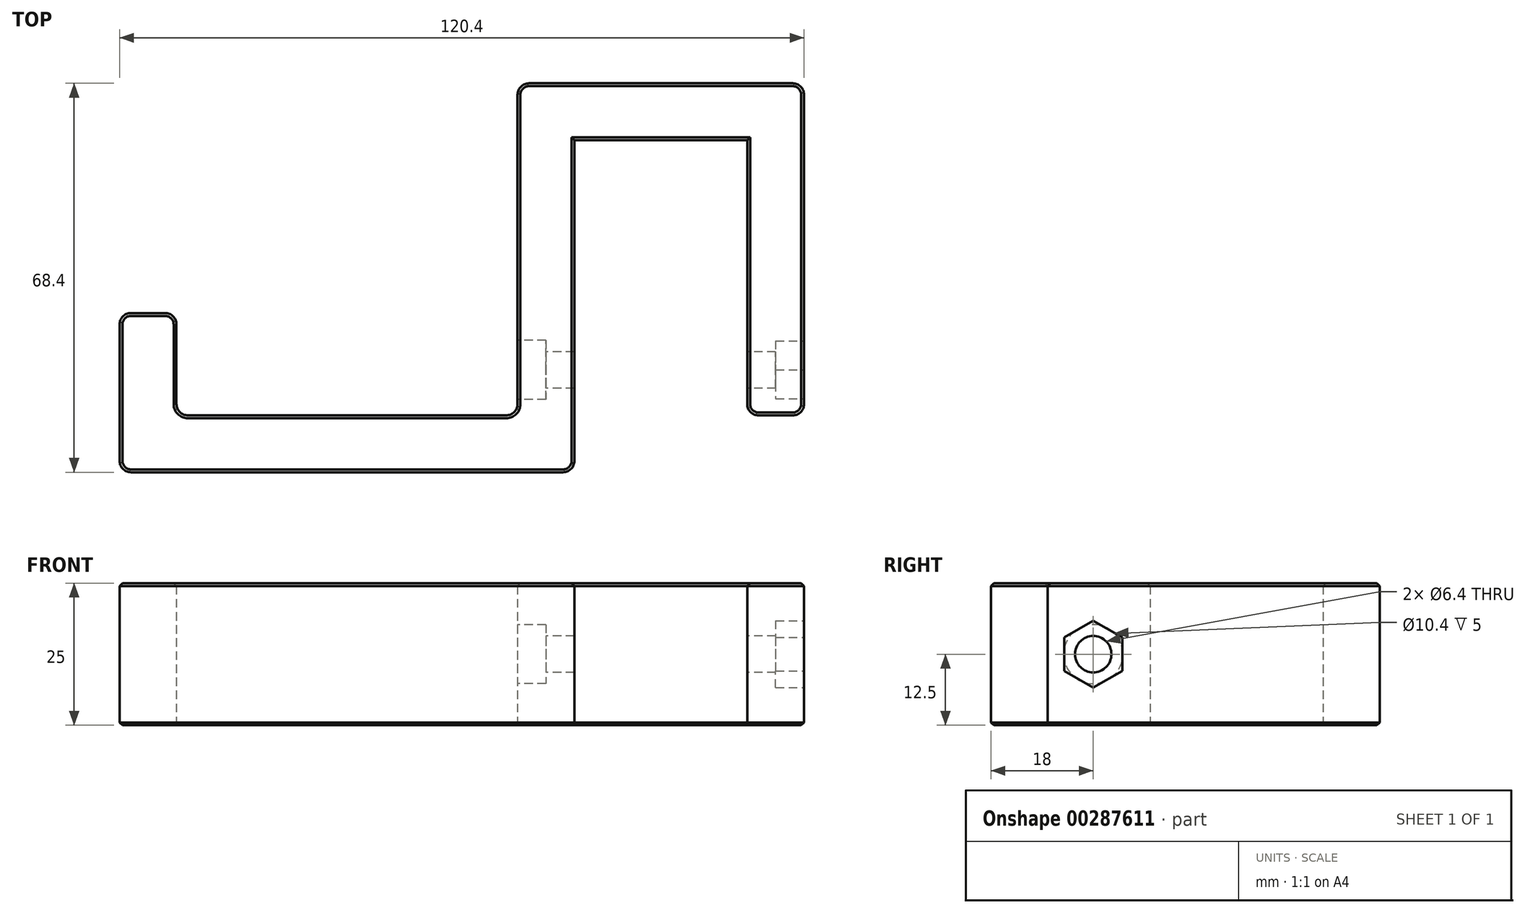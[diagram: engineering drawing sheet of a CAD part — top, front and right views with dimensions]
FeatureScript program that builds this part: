
annotation { "Feature Type Name" : "Feature", "Feature Type Description" : "" }
export const myFeature = defineFeature(function(context is Context, id is Id, definition is map)
    precondition{}
    {
        {
            var Q0;
            Q0=qCreatedBy(makeId("Top.planeOp"),FACE);
            var sketch = newSketch(context, id + "F0", { "sketchPlane" : qUnion([Q0])});
            skLineSegment(sketch, "E0.bottom", {"start": v(15.2, -15.2) * mm, "end": v(-15.2, -15.2) * mm, "construction": true});
            skLineSegment(sketch, "E0.top", {"start": v(15.2, 15.2) * mm, "end": v(-15.2, 15.2) * mm, "construction": true});
            skLineSegment(sketch, "E0.left", {"start": v(15.2, -15.2) * mm, "end": v(15.2, 15.2) * mm, "construction": true});
            skLineSegment(sketch, "E0.right", {"start": v(-15.2, -15.2) * mm, "end": v(-15.2, 15.2) * mm, "construction": true});
            skPoint(sketch, "E0.middle", {"position": v(0, 0) * mm});
            skLineSegment(sketch, "E1", {"start": v(15.2, 15.2) * mm, "end": v(15.2, -33.2) * mm});
            skLineSegment(sketch, "E2", {"start": v(15.2, -33.2) * mm, "end": v(25.2, -33.2) * mm});
            skLineSegment(sketch, "E3", {"start": v(25.2, -33.2) * mm, "end": v(25.2, 25.2) * mm});
            skLineSegment(sketch, "E4", {"start": v(25.2, 25.2) * mm, "end": v(-25.2, 25.2) * mm});
            skLineSegment(sketch, "E5", {"start": v(-25.2, 25.2) * mm, "end": v(-25.2, -33.2) * mm});
            skLineSegment(sketch, "E6", {"start": v(-25.2, -33.2) * mm, "end": v(-15.2, -33.2) * mm});
            skLineSegment(sketch, "E7", {"start": v(-15.2, -33.2) * mm, "end": v(-15.2, 15.2) * mm});
            skLineSegment(sketch, "E8.bottom", {"start": v(-15.2, -33.2) * mm, "end": v(-95.2, -33.2) * mm});
            skLineSegment(sketch, "E8.top", {"start": v(-15.2, -43.2) * mm, "end": v(-95.2, -43.2) * mm});
            skLineSegment(sketch, "E8.left", {"start": v(-15.2, -33.2) * mm, "end": v(-15.2, -43.2) * mm});
            skLineSegment(sketch, "E8.right", {"start": v(-95.2, -33.2) * mm, "end": v(-95.2, -43.2) * mm});
            skLineSegment(sketch, "E9.bottom", {"start": v(-95.2, -33.2) * mm, "end": v(-85.2, -33.2) * mm});
            skLineSegment(sketch, "E9.top", {"start": v(-95.2, -15.2) * mm, "end": v(-85.2, -15.2) * mm});
            skLineSegment(sketch, "E9.left", {"start": v(-95.2, -33.2) * mm, "end": v(-95.2, -15.2) * mm});
            skLineSegment(sketch, "E9.right", {"start": v(-85.2, -33.2) * mm, "end": v(-85.2, -15.2) * mm});
            skLineSegment(sketch, "E10", {"start": v(-15.2, 15.2) * mm, "end": v(15.2, 15.2) * mm});
            skSolve(sketch);
        }
        {
            var Q0;
            Q0=qSketchRegion(id+"F0",true);
            extrude(context, id + "F1", {"entities" : qUnion([Q0]), "depth" : 25 * mm, "offsetDistance" : 25 * mm});
        }
        {
            var Q0;
            Q0=makeQuery(id+"F1.opExtrude","SWEPT_FACE",FACE,{"disambiguationData":[OSD([sQuery(id+"F0.wireOp",EDGE,"E5")])]});
            var sketch = newSketch(context, id + "F2", { "sketchPlane" : qUnion([Q0])});
            skPoint(sketch, "E11", {"position": v(33.2, 12.5) * mm});
            skCircle(sketch, "E12", {"center": v(25.2, 12.5) * mm, "radius": 3.2 * mm});
            skCircle(sketch, "E13", {"center": v(25.2, 12.5) * mm, "radius": 5.2 * mm});
            skSolve(sketch);
        }
        {
            var Q0;
            Q0=makeQuery(id+"F2.imprint","IMPRINT",FACE,{"disambiguationData":[TD([[makeQuery(id+"F2.imprint","IMPRINT",EDGE,{"derivedFrom":sQuery(id+"F2.wireOp",EDGE,"E12")}),1.0]])]});
            extrude(context, id + "F3", {"entities" : qUnion([Q0]), "operationType" : NewBodyOperationType.REMOVE, "endBound" : BoundingType.THROUGH_ALL, "oppositeDirection" : true, "depth" : 25 * mm, "offsetDistance" : 25 * mm});
        }
        {
            var Q0;
            Q0=makeQuery(id+"F2.imprint","IMPRINT",FACE,{"disambiguationData":[TD([[makeQuery(id+"F2.imprint","IMPRINT",EDGE,{"derivedFrom":sQuery(id+"F2.wireOp",EDGE,"E12")}),-1.0]])]});
            extrude(context, id + "F4", {"entities" : qUnion([Q0]), "operationType" : NewBodyOperationType.REMOVE, "oppositeDirection" : true, "depth" : 5 * mm, "offsetDistance" : 25 * mm});
        }
        {
            var Q0;
            Q0=makeQuery(id+"F1.opExtrude","SWEPT_FACE",FACE,{"disambiguationData":[OSD([sQuery(id+"F0.wireOp",EDGE,"E3")])]});
            var sketch = newSketch(context, id + "F5", { "sketchPlane" : qUnion([Q0])});
            skCircle(sketch, "E14.cCircle", {"center": v(-25.2, 12.5) * mm, "radius": 5.1 * mm, "construction": true});
            skLineSegment(sketch, "E14.0", {"start": v(-25.2, 6.61) * mm, "end": v(-30.3, 9.56) * mm});
            skLineSegment(sketch, "E14.1", {"start": v(-30.3, 9.56) * mm, "end": v(-30.3, 15.44) * mm});
            skLineSegment(sketch, "E14.2", {"start": v(-30.3, 15.44) * mm, "end": v(-25.2, 18.39) * mm});
            skLineSegment(sketch, "E14.3", {"start": v(-25.2, 18.39) * mm, "end": v(-20.1, 15.44) * mm});
            skLineSegment(sketch, "E14.4", {"start": v(-20.1, 15.44) * mm, "end": v(-20.1, 9.56) * mm});
            skLineSegment(sketch, "E14.5", {"start": v(-20.1, 9.56) * mm, "end": v(-25.2, 6.61) * mm});
            skPoint(sketch, "E14.0.midPoint", {"position": v(-27.75, 8.08) * mm});
            skSolve(sketch);
        }
        {
            var Q0;
            Q0=makeQuery(id+"F5.imprint","IMPRINT",FACE,{"disambiguationData":[TD([[makeQuery(id+"F5.imprint","IMPRINT",EDGE,{"derivedFrom":sQuery(id+"F5.wireOp",EDGE,"E14.0")}),-1.0]])]});
            extrude(context, id + "F6", {"entities" : qUnion([Q0]), "operationType" : NewBodyOperationType.REMOVE, "oppositeDirection" : true, "depth" : 5 * mm, "offsetDistance" : 25 * mm});
        }
        {
            var Q0;
            Q0=makeQuery(id+"F1.opExtrude","SWEPT_EDGE",EDGE,{"disambiguationData":[OSD([sQuery(id+"F0.wireOp",EDGE,"E5"),sQuery(id+"F0.wireOp",EDGE,"E8.bottom")])]});
            var Q1;
            Q1=makeQuery(id+"F1.opExtrude","SWEPT_EDGE",EDGE,{"disambiguationData":[OSD([sQuery(id+"F0.wireOp",EDGE,"E8.top"),sQuery(id+"F0.wireOp",EDGE,"E8.left")])]});
            var Q2;
            Q2=makeQuery(id+"F1.opExtrude","SWEPT_EDGE",EDGE,{"disambiguationData":[OSD([sQuery(id+"F0.wireOp",EDGE,"E2"),sQuery(id+"F0.wireOp",EDGE,"E1")])]});
            var Q3;
            Q3=makeQuery(id+"F1.opExtrude","SWEPT_EDGE",EDGE,{"disambiguationData":[OSD([sQuery(id+"F0.wireOp",EDGE,"E2"),sQuery(id+"F0.wireOp",EDGE,"E3")])]});
            var Q4;
            Q4=makeQuery(id+"F1.opExtrude","SWEPT_EDGE",EDGE,{"disambiguationData":[OSD([sQuery(id+"F0.wireOp",EDGE,"E3"),sQuery(id+"F0.wireOp",EDGE,"E4")])]});
            var Q5;
            Q5=makeQuery(id+"F1.opExtrude","SWEPT_EDGE",EDGE,{"disambiguationData":[OSD([sQuery(id+"F0.wireOp",EDGE,"E8.bottom"),sQuery(id+"F0.wireOp",EDGE,"E9.bottom"),sQuery(id+"F0.wireOp",EDGE,"E9.right")])]});
            var Q6;
            Q6=makeQuery(id+"F1.opExtrude","SWEPT_EDGE",EDGE,{"disambiguationData":[OSD([sQuery(id+"F0.wireOp",EDGE,"E9.top"),sQuery(id+"F0.wireOp",EDGE,"E9.right")])]});
            var Q7;
            Q7=makeQuery(id+"F1.opExtrude","SWEPT_EDGE",EDGE,{"disambiguationData":[OSD([sQuery(id+"F0.wireOp",EDGE,"E9.top"),sQuery(id+"F0.wireOp",EDGE,"E9.left")])]});
            var Q8;
            Q8=makeQuery(id+"F1.opExtrude","SWEPT_EDGE",EDGE,{"disambiguationData":[OSD([sQuery(id+"F0.wireOp",EDGE,"E8.top"),sQuery(id+"F0.wireOp",EDGE,"E8.right")])]});
            var Q9;
            Q9=makeQuery(id+"F1.opExtrude","SWEPT_EDGE",EDGE,{"disambiguationData":[OSD([sQuery(id+"F0.wireOp",EDGE,"E4"),sQuery(id+"F0.wireOp",EDGE,"E5")])]});
            fillet(context, id + "F7", {"entities" : qUnion([Q0, Q1, Q2, Q3, Q4, Q5, Q6, Q7, Q8, Q9]), "tangentPropagation" : true, "radius" : 2 * mm, "defaultsChanged" : false, "vertexSettings" : [], "allowEdgeOverflow" : false});
        }
        {
            var Q0;
            Q0=makeQuery(id+"F1.opExtrude","CAP_FACE",FACE,{"disambiguationData":[OSD([sQuery(id+"F0.wireOp",EDGE,"E2"),sQuery(id+"F0.wireOp",EDGE,"E3"),sQuery(id+"F0.wireOp",EDGE,"E4"),sQuery(id+"F0.wireOp",EDGE,"E5"),sQuery(id+"F0.wireOp",EDGE,"E7"),sQuery(id+"F0.wireOp",EDGE,"E1"),sQuery(id+"F0.wireOp",EDGE,"E8.bottom"),sQuery(id+"F0.wireOp",EDGE,"E8.top"),sQuery(id+"F0.wireOp",EDGE,"E8.left"),sQuery(id+"F0.wireOp",EDGE,"E8.right"),sQuery(id+"F0.wireOp",EDGE,"E9.top"),sQuery(id+"F0.wireOp",EDGE,"E9.left"),sQuery(id+"F0.wireOp",EDGE,"E9.right"),sQuery(id+"F0.wireOp",EDGE,"E10")])],"isStart":false});
            var Q1;
            Q1=makeQuery(id+"F1.opExtrude","CAP_FACE",FACE,{"disambiguationData":[OSD([sQuery(id+"F0.wireOp",EDGE,"E2"),sQuery(id+"F0.wireOp",EDGE,"E3"),sQuery(id+"F0.wireOp",EDGE,"E4"),sQuery(id+"F0.wireOp",EDGE,"E5"),sQuery(id+"F0.wireOp",EDGE,"E7"),sQuery(id+"F0.wireOp",EDGE,"E1"),sQuery(id+"F0.wireOp",EDGE,"E8.bottom"),sQuery(id+"F0.wireOp",EDGE,"E8.top"),sQuery(id+"F0.wireOp",EDGE,"E8.left"),sQuery(id+"F0.wireOp",EDGE,"E8.right"),sQuery(id+"F0.wireOp",EDGE,"E9.top"),sQuery(id+"F0.wireOp",EDGE,"E9.left"),sQuery(id+"F0.wireOp",EDGE,"E9.right"),sQuery(id+"F0.wireOp",EDGE,"E10")])],"isStart":true});
            chamfer(context, id + "F8", {"entities" : qUnion([Q0, Q1]), "width" : 0.5 * mm, "tangentPropagation" : true});
        }
    });
